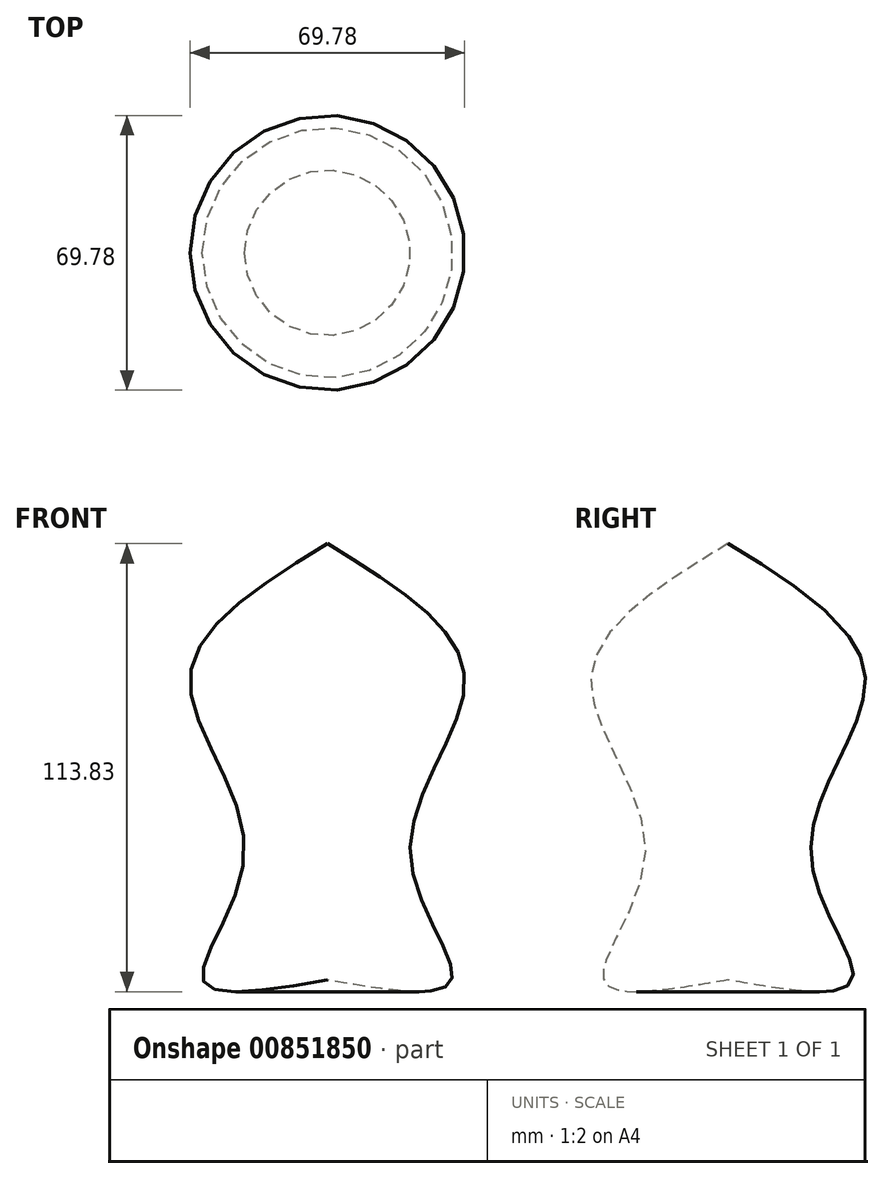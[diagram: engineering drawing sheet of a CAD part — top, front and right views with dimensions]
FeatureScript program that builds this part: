
annotation { "Feature Type Name" : "Feature", "Feature Type Description" : "" }
export const myFeature = defineFeature(function(context is Context, id is Id, definition is map)
    precondition{}
    {
        {
            var Q0;
            Q0=qCreatedBy(makeId("Front.planeOp"),FACE);
            var sketch = newSketch(context, id + "F0", { "sketchPlane" : qUnion([Q0])});
            skFitSpline(sketch, "E0", {"points": [v(0, -55.5) * mm, v(-31.58, -55.5) * mm, v(-21.05, -23.25) * mm, v(-34.87, 21.17) * mm, v(0, 55.39) * mm], "startDerivative": vector(-200.13, -34.38) * mm, "endDerivative": vector(185.5, 113.36) * mm});
            skLineSegment(sketch, "E1", {"start": v(0, 55.39) * mm, "end": v(0, -55.5) * mm});
            skSolve(sketch);
        }
        {
            var Q0;
            Q0=makeQuery(id+"F0.imprint","IMPRINT",FACE,{"disambiguationData":[TD([[makeQuery(id+"F0.imprint","IMPRINT",EDGE,{"derivedFrom":sQuery(id+"F0.wireOp",EDGE,"E0")}),-1.0]])]});
            var Q1;
            Q1=sQuery(id+"F0.wireOp",EDGE,"E1");
            revolve(context, id + "F1", {"surfaceOperationType" : NewSurfaceOperationType.NEW, "entities" : qUnion([Q0]), "axis" : qUnion([Q1]), "revolveType" : RevolveType.FULL});
        }
    });
